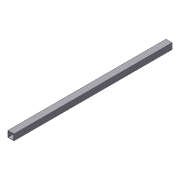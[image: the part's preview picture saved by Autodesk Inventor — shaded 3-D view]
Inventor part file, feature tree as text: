
AUTODESK INVENTOR PART (.ipt)
format: ipt  version: 2012 (Build 160160000, 160)  size: 71,680 bytes
history: native  units: in
note: dims shown in document units (in); Inventor stores cm internally (conversion verified against a paired STEP export)
features: extrude x1, shell x1, sketch x1
ambient origin geometry x8: Origin, YZ Plane, XZ Plane, XY Plane, X Axis, Y Axis, Z Axis, Center Point
bodies: Solid1 (feature_tree)
feature tree (3):
  extrude  "Extrusion1"  Depth=1.0in
  shell  "Shell1"  Thickness=26.0in
  sketch  "Sketch1"  dims[d0=1.0in d1=1.0in d2=26.0in d3=0.0in d4=0.0625in]
